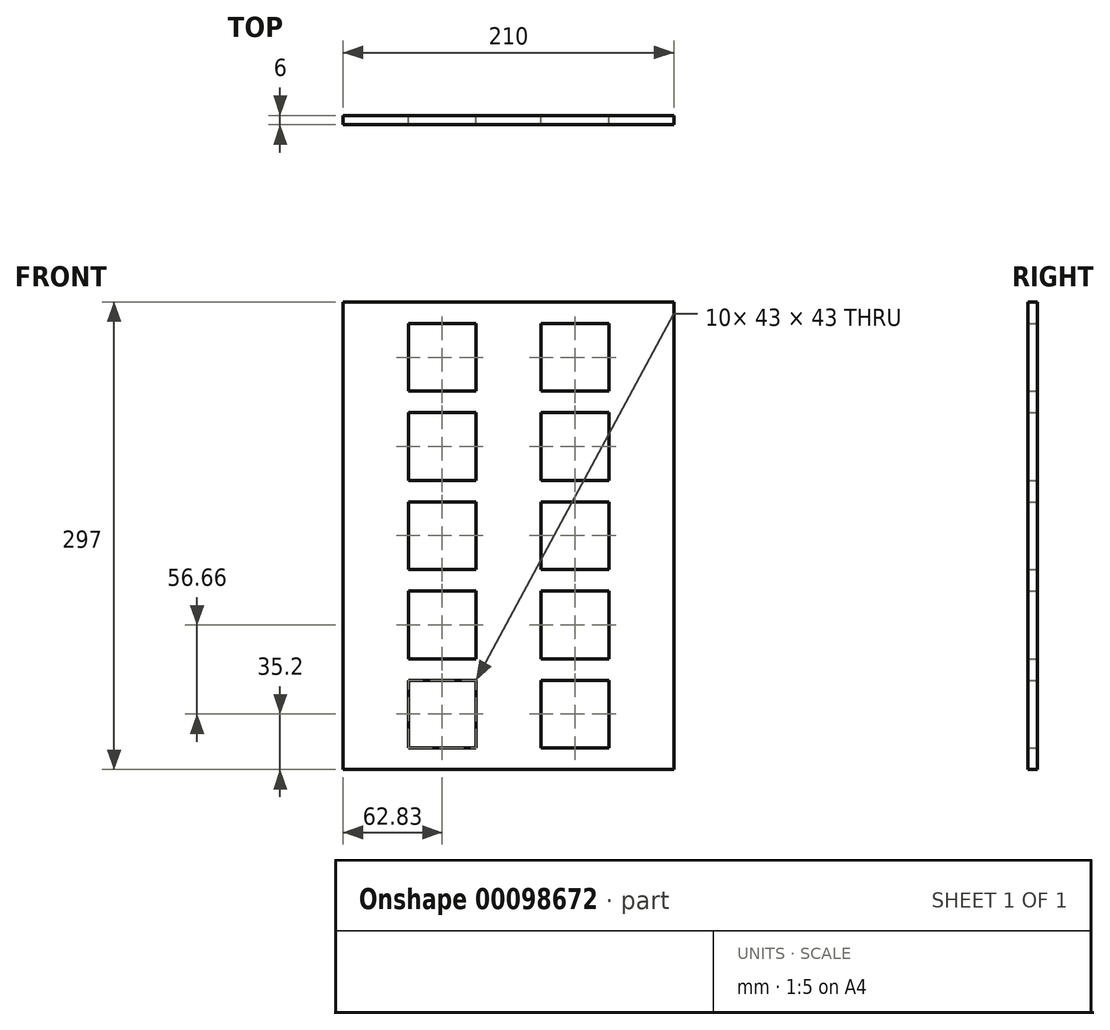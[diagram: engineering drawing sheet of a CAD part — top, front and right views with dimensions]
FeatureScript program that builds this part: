
annotation { "Feature Type Name" : "Feature", "Feature Type Description" : "" }
export const myFeature = defineFeature(function(context is Context, id is Id, definition is map)
    precondition{}
    {
        {
            var Q0;
            Q0=qCreatedBy(makeId("Front.planeOp"),FACE);
            var sketch = newSketch(context, id + "F0", { "sketchPlane" : qUnion([Q0])});
            skLineSegment(sketch, "E0.bottom", {"start": v(105, -148.5) * mm, "end": v(-105, -148.5) * mm});
            skLineSegment(sketch, "E0.top", {"start": v(105, 148.5) * mm, "end": v(-105, 148.5) * mm});
            skLineSegment(sketch, "E0.left", {"start": v(105, -148.5) * mm, "end": v(105, 148.5) * mm});
            skLineSegment(sketch, "E0.right", {"start": v(-105, -148.5) * mm, "end": v(-105, 148.5) * mm});
            skPoint(sketch, "E0.middle", {"position": v(0, 0) * mm});
            skLineSegment(sketch, "E1.bottom", {"start": v(-20.67, 91.84) * mm, "end": v(-63.67, 91.84) * mm});
            skLineSegment(sketch, "E1.top", {"start": v(-20.67, 134.84) * mm, "end": v(-63.67, 134.84) * mm});
            skLineSegment(sketch, "E1.left", {"start": v(-20.67, 91.84) * mm, "end": v(-20.67, 134.84) * mm});
            skLineSegment(sketch, "E1.right", {"start": v(-63.67, 91.84) * mm, "end": v(-63.67, 134.84) * mm});
            skPoint(sketch, "E1.middle", {"position": v(-42.17, 113.34) * mm});
            skLineSegment(sketch, "E2.0.1.0", {"start": v(-20.67, 78.18) * mm, "end": v(-63.67, 78.18) * mm});
            skLineSegment(sketch, "E2.0.1.1", {"start": v(-20.67, 35.18) * mm, "end": v(-63.67, 35.18) * mm});
            skLineSegment(sketch, "E2.0.1.2", {"start": v(-63.67, 35.18) * mm, "end": v(-63.67, 78.18) * mm});
            skLineSegment(sketch, "E2.0.1.3", {"start": v(-20.67, 35.18) * mm, "end": v(-20.67, 78.18) * mm});
            skLineSegment(sketch, "E2.0.2.0", {"start": v(-20.67, 21.52) * mm, "end": v(-63.67, 21.52) * mm});
            skLineSegment(sketch, "E2.0.2.1", {"start": v(-20.67, -21.48) * mm, "end": v(-63.67, -21.48) * mm});
            skLineSegment(sketch, "E2.0.2.2", {"start": v(-63.67, -21.48) * mm, "end": v(-63.67, 21.52) * mm});
            skLineSegment(sketch, "E2.0.2.3", {"start": v(-20.67, -21.48) * mm, "end": v(-20.67, 21.52) * mm});
            skLineSegment(sketch, "E2.0.3.0", {"start": v(-20.67, -35.14) * mm, "end": v(-63.67, -35.14) * mm});
            skLineSegment(sketch, "E2.0.3.1", {"start": v(-20.67, -78.14) * mm, "end": v(-63.67, -78.14) * mm});
            skLineSegment(sketch, "E2.0.3.2", {"start": v(-63.67, -78.14) * mm, "end": v(-63.67, -35.14) * mm});
            skLineSegment(sketch, "E2.0.3.3", {"start": v(-20.67, -78.14) * mm, "end": v(-20.67, -35.14) * mm});
            skLineSegment(sketch, "E2.0.4.0", {"start": v(-20.67, -91.8) * mm, "end": v(-63.67, -91.8) * mm});
            skLineSegment(sketch, "E2.0.4.1", {"start": v(-20.67, -134.8) * mm, "end": v(-63.67, -134.8) * mm});
            skLineSegment(sketch, "E2.0.4.2", {"start": v(-63.67, -134.8) * mm, "end": v(-63.67, -91.8) * mm});
            skLineSegment(sketch, "E2.0.4.3", {"start": v(-20.67, -134.8) * mm, "end": v(-20.67, -91.8) * mm});
            skLineSegment(sketch, "E2.1.0.0", {"start": v(63.66, 134.84) * mm, "end": v(20.66, 134.84) * mm});
            skLineSegment(sketch, "E2.1.0.1", {"start": v(63.66, 91.84) * mm, "end": v(20.66, 91.84) * mm});
            skLineSegment(sketch, "E2.1.0.2", {"start": v(20.66, 91.84) * mm, "end": v(20.66, 134.84) * mm});
            skLineSegment(sketch, "E2.1.0.3", {"start": v(63.66, 91.84) * mm, "end": v(63.66, 134.84) * mm});
            skLineSegment(sketch, "E2.1.1.0", {"start": v(63.66, 78.18) * mm, "end": v(20.66, 78.18) * mm});
            skLineSegment(sketch, "E2.1.1.1", {"start": v(63.66, 35.18) * mm, "end": v(20.66, 35.18) * mm});
            skLineSegment(sketch, "E2.1.1.2", {"start": v(20.66, 35.18) * mm, "end": v(20.66, 78.18) * mm});
            skLineSegment(sketch, "E2.1.1.3", {"start": v(63.66, 35.18) * mm, "end": v(63.66, 78.18) * mm});
            skLineSegment(sketch, "E2.1.2.0", {"start": v(63.66, 21.52) * mm, "end": v(20.66, 21.52) * mm});
            skLineSegment(sketch, "E2.1.2.1", {"start": v(63.66, -21.48) * mm, "end": v(20.66, -21.48) * mm});
            skLineSegment(sketch, "E2.1.2.2", {"start": v(20.66, -21.48) * mm, "end": v(20.66, 21.52) * mm});
            skLineSegment(sketch, "E2.1.2.3", {"start": v(63.66, -21.48) * mm, "end": v(63.66, 21.52) * mm});
            skLineSegment(sketch, "E2.1.3.0", {"start": v(63.66, -35.14) * mm, "end": v(20.66, -35.14) * mm});
            skLineSegment(sketch, "E2.1.3.1", {"start": v(63.66, -78.14) * mm, "end": v(20.66, -78.14) * mm});
            skLineSegment(sketch, "E2.1.3.2", {"start": v(20.66, -78.14) * mm, "end": v(20.66, -35.14) * mm});
            skLineSegment(sketch, "E2.1.3.3", {"start": v(63.66, -78.14) * mm, "end": v(63.66, -35.14) * mm});
            skLineSegment(sketch, "E2.1.4.0", {"start": v(63.66, -91.8) * mm, "end": v(20.66, -91.8) * mm});
            skLineSegment(sketch, "E2.1.4.1", {"start": v(63.66, -134.8) * mm, "end": v(20.66, -134.8) * mm});
            skLineSegment(sketch, "E2.1.4.2", {"start": v(20.66, -134.8) * mm, "end": v(20.66, -91.8) * mm});
            skLineSegment(sketch, "E2.1.4.3", {"start": v(63.66, -134.8) * mm, "end": v(63.66, -91.8) * mm});
            skLineSegment(sketch, "E2.direction1", {"start": v(-63.7, 134.9) * mm, "end": v(20.63, 134.9) * mm, "construction": true});
            skLineSegment(sketch, "E2.direction2", {"start": v(-63.7, 134.9) * mm, "end": v(-63.7, 78.24) * mm, "construction": true});
            skSolve(sketch);
        }
        {
            var Q0;
            Q0 = qSketchRegion(id + "F0", true);
            extrude(context, id + "F1", {"entities" : qUnion([Q0]), "endBound" : BoundingType.SYMMETRIC, "depth" : 6 * mm});
        }
    });
